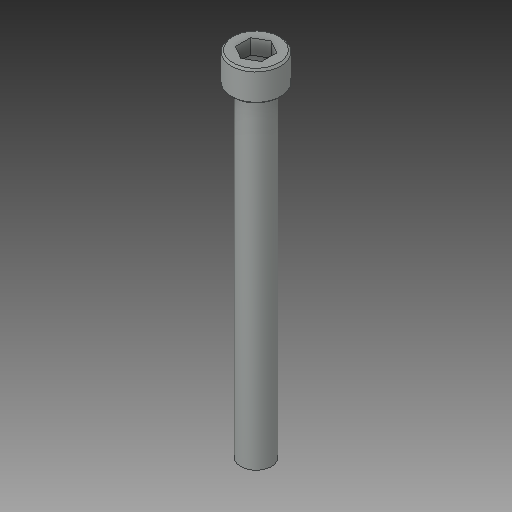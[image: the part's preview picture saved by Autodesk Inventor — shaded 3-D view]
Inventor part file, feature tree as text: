
AUTODESK INVENTOR PART (.ipt)
format: ipt  version: 2017 SP1 (Build 210196100, 196)  size: 93,184 bytes
history: native  units: in
note: dims shown in document units (in); Inventor stores cm internally (conversion verified against a paired STEP export)
features: chamfer x1
ambient origin geometry x8: Origin, YZ Plane, XZ Plane, XY Plane, X Axis, Y Axis, Z Axis, Center Point
bodies: Solid1 (feature_tree)
feature tree (1):
  chamfer  "Chamfer2"  [1 undecoded]
note: 1 required parameter value undecoded (feature->parameter linkage not recoverable at this tier; creation-order binding heuristic only, values carry confidence <= 0.55)
